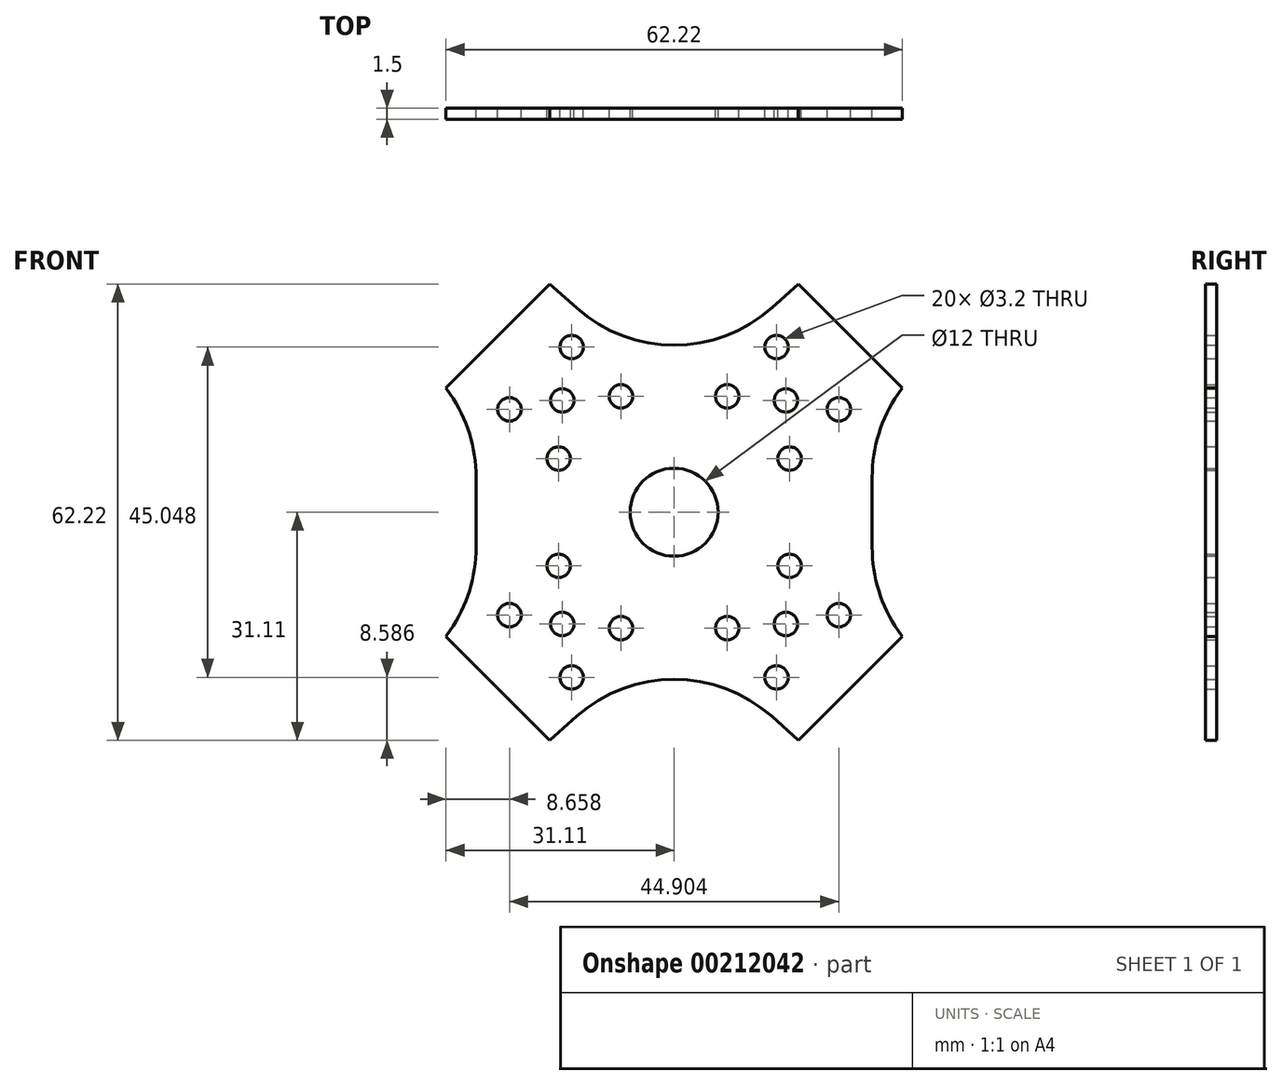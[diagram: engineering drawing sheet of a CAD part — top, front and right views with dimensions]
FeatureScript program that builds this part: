
annotation { "Feature Type Name" : "Feature", "Feature Type Description" : "" }
export const myFeature = defineFeature(function(context is Context, id is Id, definition is map)
    precondition{}
    {
        {
            var Q0;
            Q0=qCreatedBy(makeId("Front.planeOp"),FACE);
            var sketch = newSketch(context, id + "F0", { "sketchPlane" : qUnion([Q0])});
            skPoint(sketch, "E0", {"position": v(0, 0) * mm});
            skCircle(sketch, "E1", {"center": v(15.73, 7.32) * mm, "radius": 1.6 * mm});
            skCircle(sketch, "E2", {"center": v(13.97, 22.52) * mm, "radius": 1.6 * mm});
            skCircle(sketch, "E3", {"center": v(7.25, 15.8) * mm, "radius": 1.6 * mm});
            skCircle(sketch, "E4", {"center": v(22.45, 14.04) * mm, "radius": 1.6 * mm});
            skCircle(sketch, "E5", {"center": v(15.25, 15.25) * mm, "radius": 1.6 * mm});
            skCircle(sketch, "E6.MirrorC", {"center": v(15.73, -7.32) * mm, "radius": 1.6 * mm});
            skCircle(sketch, "E7.MirrorC", {"center": v(15.25, -15.25) * mm, "radius": 1.6 * mm});
            skCircle(sketch, "E8.MirrorC", {"center": v(22.45, -14.04) * mm, "radius": 1.6 * mm});
            skCircle(sketch, "E9.MirrorC", {"center": v(7.25, -15.8) * mm, "radius": 1.6 * mm});
            skCircle(sketch, "E10.MirrorC", {"center": v(13.97, -22.52) * mm, "radius": 1.6 * mm});
            skCircle(sketch, "E11.MirrorC", {"center": v(-7.25, -15.8) * mm, "radius": 1.6 * mm});
            skCircle(sketch, "E12.MirrorC", {"center": v(-15.25, -15.25) * mm, "radius": 1.6 * mm});
            skCircle(sketch, "E13.MirrorC", {"center": v(-22.45, -14.04) * mm, "radius": 1.6 * mm});
            skCircle(sketch, "E14.MirrorC", {"center": v(-13.97, 22.52) * mm, "radius": 1.6 * mm});
            skCircle(sketch, "E15.MirrorC", {"center": v(-15.25, 15.25) * mm, "radius": 1.6 * mm});
            skCircle(sketch, "E16.MirrorC", {"center": v(-15.73, -7.32) * mm, "radius": 1.6 * mm});
            skCircle(sketch, "E17.MirrorC", {"center": v(-22.45, 14.04) * mm, "radius": 1.6 * mm});
            skCircle(sketch, "E18.MirrorC", {"center": v(-13.97, -22.52) * mm, "radius": 1.6 * mm});
            skCircle(sketch, "E19.MirrorC", {"center": v(-15.73, 7.32) * mm, "radius": 1.6 * mm});
            skCircle(sketch, "E20.MirrorC", {"center": v(-7.25, 15.8) * mm, "radius": 1.6 * mm});
            skLineSegment(sketch, "E21", {"start": v(-29.28, -29.28) * mm, "end": v(35.77, 35.77) * mm, "construction": true});
            skLineSegment(sketch, "E22", {"start": v(16.97, 31.11) * mm, "end": v(31.11, 16.97) * mm});
            skPoint(sketch, "E23", {"position": v(0, 16) * mm});
            skLineSegment(sketch, "E24", {"start": v(16.97, 31.11) * mm, "end": v(13.3, 27.84) * mm});
            skLineSegment(sketch, "E25", {"start": v(27, 4.78) * mm, "end": v(27, -4.78) * mm});
            skLineSegment(sketch, "E26", {"start": v(31.11, 16.97) * mm, "end": v(30.53, 16.12) * mm});
            skLineSegment(sketch, "E27.MirrorCS", {"start": v(-27, 4.78) * mm, "end": v(-27, -4.78) * mm});
            skLineSegment(sketch, "E28.MirrorCS", {"start": v(-31.11, 16.97) * mm, "end": v(-30.53, 16.12) * mm});
            skLineSegment(sketch, "E29.MirrorCS", {"start": v(-16.97, 31.11) * mm, "end": v(-13.3, 27.84) * mm});
            skLineSegment(sketch, "E30.MirrorCS", {"start": v(-16.97, 31.11) * mm, "end": v(-31.11, 16.97) * mm});
            skArc(sketch, "E31.filletArc", {"start": v(-13.3, 27.84) * mm, "mid": v(0, 22.78) * mm, "end": v(13.3, 27.84) * mm});
            skPoint(sketch, "E32.visualSharp", {"position": v(27, 11) * mm});
            skArc(sketch, "E32.filletArc", {"start": v(30.53, 16.12) * mm, "mid": v(27.9, 10.72) * mm, "end": v(27, 4.78) * mm});
            skPoint(sketch, "E33.visualSharp", {"position": v(-27, 11) * mm});
            skArc(sketch, "E33.filletArc", {"start": v(-27, 4.78) * mm, "mid": v(-27.9, 10.72) * mm, "end": v(-30.53, 16.12) * mm});
            skArc(sketch, "E34.MirrorCS", {"start": v(30.53, -16.12) * mm, "mid": v(27.9, -10.72) * mm, "end": v(27, -4.78) * mm});
            skLineSegment(sketch, "E35.MirrorCS", {"start": v(31.11, -16.97) * mm, "end": v(30.53, -16.12) * mm});
            skLineSegment(sketch, "E36.MirrorCS", {"start": v(16.97, -31.11) * mm, "end": v(31.11, -16.97) * mm});
            skLineSegment(sketch, "E37.MirrorCS", {"start": v(16.97, -31.11) * mm, "end": v(13.3, -27.84) * mm});
            skArc(sketch, "E38.MirrorCS", {"start": v(-13.3, -27.84) * mm, "mid": v(0, -22.78) * mm, "end": v(13.3, -27.84) * mm});
            skLineSegment(sketch, "E39.MirrorCS", {"start": v(-16.97, -31.11) * mm, "end": v(-13.3, -27.84) * mm});
            skLineSegment(sketch, "E40.MirrorCS", {"start": v(-31.11, -16.97) * mm, "end": v(-30.53, -16.12) * mm});
            skLineSegment(sketch, "E41.MirrorCS", {"start": v(-16.97, -31.11) * mm, "end": v(-31.11, -16.97) * mm});
            skArc(sketch, "E42.MirrorCS", {"start": v(-27, -4.78) * mm, "mid": v(-27.9, -10.72) * mm, "end": v(-30.53, -16.12) * mm});
            skPoint(sketch, "E43.orphan", {"position": v(27, -11) * mm});
            skPoint(sketch, "E44.orphan", {"position": v(-27, -11) * mm});
            skCircle(sketch, "E45", {"center": v(0, 0) * mm, "radius": 6 * mm});
            skSolve(sketch);
        }
        {
            var Q0;
            Q0 = qSketchRegion(id + "F0", true);
            extrude(context, id + "F1", {"entities" : qUnion([Q0]), "depth" : 1.5 * mm});
        }
    });
